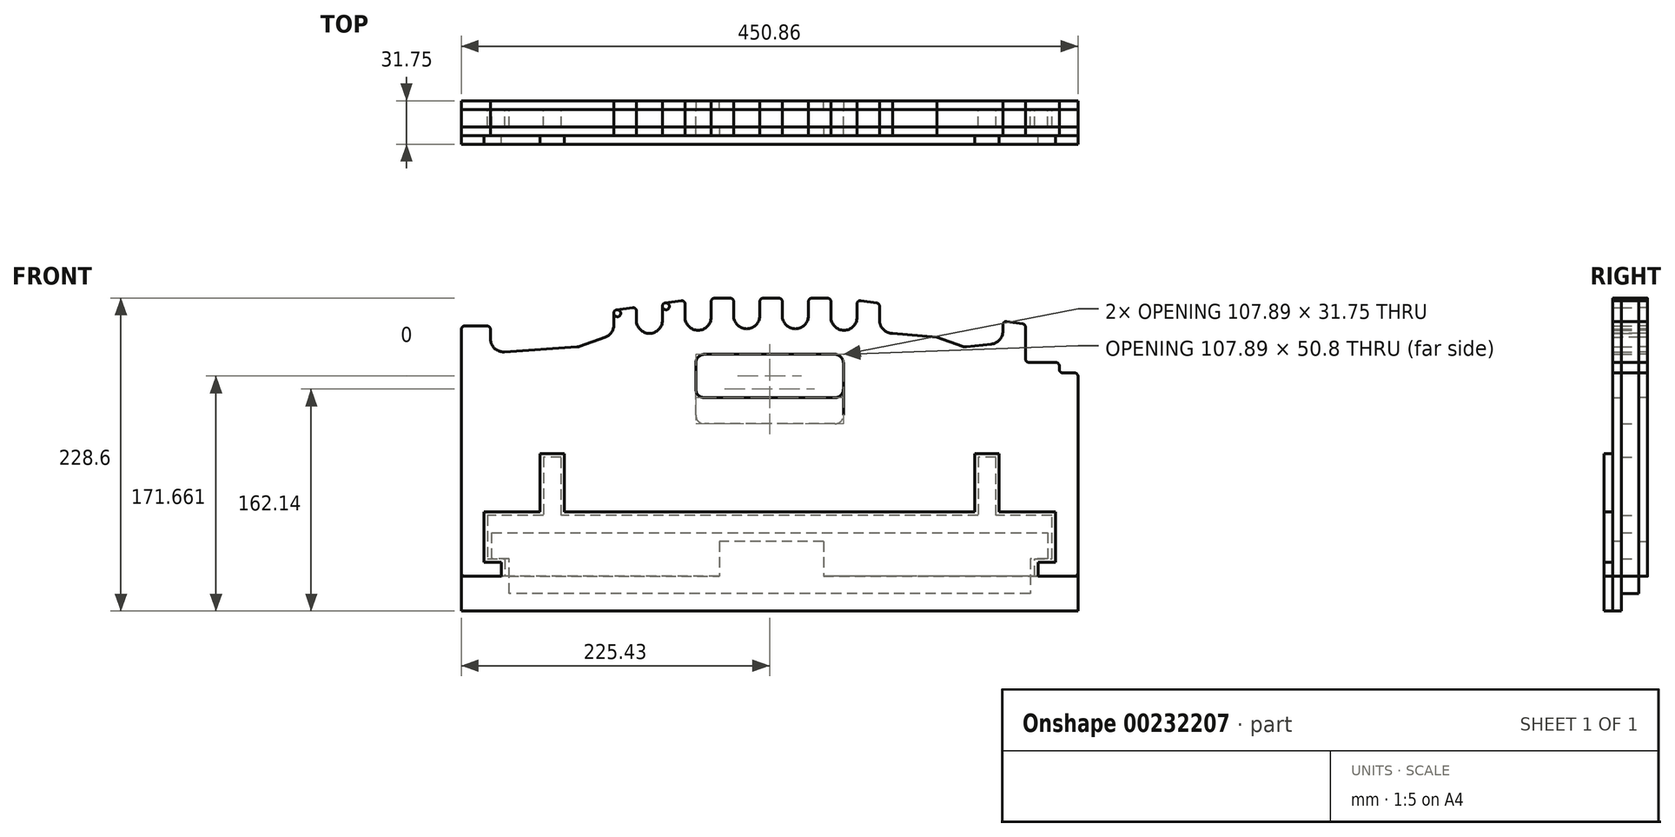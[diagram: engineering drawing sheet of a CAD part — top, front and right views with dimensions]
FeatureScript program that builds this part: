
annotation { "Feature Type Name" : "Feature", "Feature Type Description" : "" }
export const myFeature = defineFeature(function(context is Context, id is Id, definition is map)
    precondition{}
    {
        {
            var Q0;
            Q0=qCreatedBy(makeId("Front.planeOp"),FACE);
            var sketch = newSketch(context, id + "F0", { "sketchPlane" : qUnion([Q0])});
            skLineSegment(sketch, "E0", {"start": v(225.43, 44.45) * mm, "end": v(225.43, -101.6) * mm});
            skArc(sketch, "E1", {"start": v(225.42, 44.45) * mm, "mid": v(224.68, 46.25) * mm, "end": v(222.88, 47) * mm});
            skLineSegment(sketch, "E2", {"start": v(214.35, 47) * mm, "end": v(222.88, 47) * mm});
            skArc(sketch, "E3", {"start": v(211.8, 49.53) * mm, "mid": v(212.55, 47.73) * mm, "end": v(214.35, 47) * mm});
            skLineSegment(sketch, "E4", {"start": v(211.8, 52.07) * mm, "end": v(211.8, 49.53) * mm});
            skArc(sketch, "E5", {"start": v(211.8, 52.07) * mm, "mid": v(211.06, 53.87) * mm, "end": v(209.27, 54.6) * mm});
            skLineSegment(sketch, "E6", {"start": v(189.61, 54.61) * mm, "end": v(209.27, 54.61) * mm});
            skArc(sketch, "E7", {"start": v(187.07, 57.15) * mm, "mid": v(187.81, 55.35) * mm, "end": v(189.61, 54.61) * mm});
            skLineSegment(sketch, "E8", {"start": v(187.07, 80.43) * mm, "end": v(187.07, 57.15) * mm});
            skArc(sketch, "E9", {"start": v(187.07, 80.43) * mm, "mid": v(186.45, 82.1) * mm, "end": v(184.9, 82.94) * mm});
            skLineSegment(sketch, "E10", {"start": v(173.46, 84.58) * mm, "end": v(184.9, 82.94) * mm});
            skArc(sketch, "E11", {"start": v(173.46, 84.58) * mm, "mid": v(171.44, 83.98) * mm, "end": v(170.56, 82.06) * mm});
            skLineSegment(sketch, "E12", {"start": v(170.56, 77.52) * mm, "end": v(170.56, 82.06) * mm});
            skArc(sketch, "E13", {"start": v(162.11, 68.05) * mm, "mid": v(168.14, 71.17) * mm, "end": v(170.56, 77.52) * mm});
            skLineSegment(sketch, "E14", {"start": v(143.97, 65.99) * mm, "end": v(162.11, 68.05) * mm});
            skArc(sketch, "E15", {"start": v(141.12, 66.32) * mm, "mid": v(142.53, 65.99) * mm, "end": v(143.97, 65.99) * mm});
            skLineSegment(sketch, "E16", {"start": v(122.27, 73.06) * mm, "end": v(141.12, 66.32) * mm});
            skArc(sketch, "E17", {"start": v(115.95, 82.03) * mm, "mid": v(117.69, 76.54) * mm, "end": v(122.27, 73.06) * mm});
            skLineSegment(sketch, "E18", {"start": v(115.95, 90.6) * mm, "end": v(115.95, 82.03) * mm});
            skArc(sketch, "E19", {"start": v(115.95, 90.6) * mm, "mid": v(115.33, 92.26) * mm, "end": v(113.77, 93.1) * mm});
            skLineSegment(sketch, "E20", {"start": v(102.34, 94.74) * mm, "end": v(113.77, 93.1) * mm});
            skArc(sketch, "E21", {"start": v(102.34, 94.74) * mm, "mid": v(100.32, 94.14) * mm, "end": v(99.44, 92.22) * mm});
            skLineSegment(sketch, "E22", {"start": v(99.44, 85.4) * mm, "end": v(99.44, 92.22) * mm});
            skArc(sketch, "E23", {"start": v(80.4, 85.4) * mm, "mid": v(89.92, 75.87) * mm, "end": v(99.44, 85.4) * mm});
            skLineSegment(sketch, "E24", {"start": v(80.4, 95.67) * mm, "end": v(80.4, 85.4) * mm});
            skArc(sketch, "E25", {"start": v(80.4, 95.67) * mm, "mid": v(79.77, 97.34) * mm, "end": v(78.21, 98.19) * mm});
            skLineSegment(sketch, "E26", {"start": v(66.78, 99.82) * mm, "end": v(78.21, 98.19) * mm});
            skArc(sketch, "E27", {"start": v(66.78, 99.82) * mm, "mid": v(64.76, 99.22) * mm, "end": v(63.88, 97.3) * mm});
            skLineSegment(sketch, "E28", {"start": v(63.88, 87.64) * mm, "end": v(63.88, 97.3) * mm});
            skArc(sketch, "E29", {"start": v(44.83, 87.64) * mm, "mid": v(54.36, 78.12) * mm, "end": v(63.88, 87.64) * mm});
            skLineSegment(sketch, "E30", {"start": v(44.83, 99.06) * mm, "end": v(44.83, 87.64) * mm});
            skArc(sketch, "E31", {"start": v(44.83, 99.06) * mm, "mid": v(44.09, 100.86) * mm, "end": v(42.3, 101.6) * mm});
            skLineSegment(sketch, "E32", {"start": v(30.86, 101.6) * mm, "end": v(42.3, 101.6) * mm});
            skArc(sketch, "E33", {"start": v(30.86, 101.6) * mm, "mid": v(29.06, 100.86) * mm, "end": v(28.32, 99.06) * mm});
            skLineSegment(sketch, "E34", {"start": v(28.32, 88.76) * mm, "end": v(28.32, 99.06) * mm});
            skArc(sketch, "E35", {"start": v(9.27, 88.76) * mm, "mid": v(18.8, 79.24) * mm, "end": v(28.32, 88.76) * mm});
            skLineSegment(sketch, "E36", {"start": v(9.27, 99.06) * mm, "end": v(9.27, 88.76) * mm});
            skArc(sketch, "E37", {"start": v(9.27, 99.06) * mm, "mid": v(8.53, 100.86) * mm, "end": v(6.73, 101.6) * mm});
            skLineSegment(sketch, "E38", {"start": v(-4.7, 101.6) * mm, "end": v(6.73, 101.6) * mm});
            skArc(sketch, "E39", {"start": v(-4.7, 101.6) * mm, "mid": v(-6.5, 100.86) * mm, "end": v(-7.24, 99.06) * mm});
            skLineSegment(sketch, "E40", {"start": v(-7.24, 88.76) * mm, "end": v(-7.24, 99.06) * mm});
            skArc(sketch, "E41", {"start": v(-26.29, 88.76) * mm, "mid": v(-16.76, 79.24) * mm, "end": v(-7.24, 88.76) * mm});
            skLineSegment(sketch, "E42", {"start": v(-26.29, 99.06) * mm, "end": v(-26.29, 88.76) * mm});
            skArc(sketch, "E43", {"start": v(-26.29, 99.06) * mm, "mid": v(-27.03, 100.86) * mm, "end": v(-28.83, 101.6) * mm});
            skLineSegment(sketch, "E44", {"start": v(-40.26, 101.6) * mm, "end": v(-28.83, 101.6) * mm});
            skArc(sketch, "E45", {"start": v(-40.26, 101.6) * mm, "mid": v(-42.06, 100.86) * mm, "end": v(-42.8, 99.06) * mm});
            skLineSegment(sketch, "E46", {"start": v(-42.8, 87.64) * mm, "end": v(-42.8, 99.06) * mm});
            skArc(sketch, "E47", {"start": v(-61.85, 87.64) * mm, "mid": v(-52.32, 78.12) * mm, "end": v(-42.8, 87.64) * mm});
            skLineSegment(sketch, "E48", {"start": v(-61.85, 97.3) * mm, "end": v(-61.85, 87.64) * mm});
            skArc(sketch, "E49", {"start": v(-61.85, 97.3) * mm, "mid": v(-62.72, 99.23) * mm, "end": v(-64.75, 99.82) * mm});
            skLineSegment(sketch, "E50", {"start": v(-76.18, 98.19) * mm, "end": v(-64.75, 99.82) * mm});
            skArc(sketch, "E51", {"start": v(-76.18, 98.19) * mm, "mid": v(-77.74, 97.34) * mm, "end": v(-78.36, 95.67) * mm});
            skLineSegment(sketch, "E52", {"start": v(-78.36, 85.4) * mm, "end": v(-78.36, 95.67) * mm});
            skArc(sketch, "E53", {"start": v(-97.4, 85.4) * mm, "mid": v(-87.88, 75.87) * mm, "end": v(-78.36, 85.4) * mm});
            skLineSegment(sketch, "E54", {"start": v(-97.4, 92.23) * mm, "end": v(-97.4, 85.4) * mm});
            skArc(sketch, "E55", {"start": v(-97.4, 92.23) * mm, "mid": v(-98.28, 94.15) * mm, "end": v(-100.3, 94.74) * mm});
            skLineSegment(sketch, "E56", {"start": v(-111.74, 93.1) * mm, "end": v(-100.3, 94.74) * mm});
            skArc(sketch, "E57", {"start": v(-111.74, 93.1) * mm, "mid": v(-113.3, 92.26) * mm, "end": v(-113.92, 90.6) * mm});
            skLineSegment(sketch, "E58", {"start": v(-113.92, 82.03) * mm, "end": v(-113.92, 90.6) * mm});
            skArc(sketch, "E59", {"start": v(-120.24, 73.06) * mm, "mid": v(-115.66, 76.54) * mm, "end": v(-113.92, 82.03) * mm});
            skLineSegment(sketch, "E60", {"start": v(-139.09, 66.32) * mm, "end": v(-120.24, 73.06) * mm});
            skArc(sketch, "E61", {"start": v(-140.8, 65.96) * mm, "mid": v(-139.93, 66.08) * mm, "end": v(-139.09, 66.32) * mm});
            skLineSegment(sketch, "E62", {"start": v(-193.92, 62.35) * mm, "end": v(-140.8, 65.96) * mm});
            skArc(sketch, "E63", {"start": v(-204.09, 71.85) * mm, "mid": v(-201.07, 64.9) * mm, "end": v(-193.92, 62.35) * mm});
            skLineSegment(sketch, "E64", {"start": v(-204.09, 78.74) * mm, "end": v(-204.09, 71.85) * mm});
            skArc(sketch, "E65", {"start": v(-204.09, 78.74) * mm, "mid": v(-204.83, 80.54) * mm, "end": v(-206.63, 81.28) * mm});
            skLineSegment(sketch, "E66", {"start": v(-222.89, 81.28) * mm, "end": v(-206.63, 81.28) * mm});
            skArc(sketch, "E67", {"start": v(-222.89, 81.28) * mm, "mid": v(-224.68, 80.54) * mm, "end": v(-225.43, 78.74) * mm});
            skLineSegment(sketch, "E68", {"start": v(-225.43, -101.6) * mm, "end": v(-225.43, 78.74) * mm});
            skLineSegment(sketch, "E69", {"start": v(-193.68, -101.6) * mm, "end": v(-225.43, -101.6) * mm});
            skLineSegment(sketch, "E70", {"start": v(-193.68, -88.9) * mm, "end": v(-193.68, -101.6) * mm});
            skLineSegment(sketch, "E71", {"start": v(-206.38, -88.9) * mm, "end": v(-193.68, -88.9) * mm});
            skLineSegment(sketch, "E72", {"start": v(-206.38, -57.15) * mm, "end": v(-206.38, -88.9) * mm});
            skLineSegment(sketch, "E73", {"start": v(-165.35, -57.15) * mm, "end": v(-206.38, -57.15) * mm});
            skLineSegment(sketch, "E74", {"start": v(-165.35, -14.48) * mm, "end": v(-165.35, -57.15) * mm});
            skLineSegment(sketch, "E75", {"start": v(-152.4, -14.48) * mm, "end": v(-165.35, -14.48) * mm});
            skLineSegment(sketch, "E76", {"start": v(-152.4, -57.15) * mm, "end": v(-152.4, -14.48) * mm});
            skLineSegment(sketch, "E77", {"start": v(152.4, -57.15) * mm, "end": v(-152.4, -57.15) * mm});
            skLineSegment(sketch, "E78", {"start": v(152.4, -14.48) * mm, "end": v(152.4, -57.15) * mm});
            skLineSegment(sketch, "E79", {"start": v(165.35, -14.48) * mm, "end": v(152.4, -14.48) * mm});
            skLineSegment(sketch, "E80", {"start": v(165.35, -57.15) * mm, "end": v(165.35, -14.48) * mm});
            skLineSegment(sketch, "E81", {"start": v(206.38, -57.15) * mm, "end": v(165.35, -57.15) * mm});
            skLineSegment(sketch, "E82", {"start": v(206.38, -88.9) * mm, "end": v(206.38, -57.15) * mm});
            skLineSegment(sketch, "E83", {"start": v(193.68, -88.9) * mm, "end": v(206.38, -88.9) * mm});
            skLineSegment(sketch, "E84", {"start": v(193.68, -101.6) * mm, "end": v(193.68, -88.9) * mm});
            skLineSegment(sketch, "E85", {"start": v(225.43, -101.6) * mm, "end": v(193.68, -101.6) * mm});
            skLineSegment(sketch, "E86", {"start": v(47.6, 9.74) * mm, "end": v(-47.6, 9.74) * mm});
            skArc(sketch, "E87", {"start": v(-53.95, 16.1) * mm, "mid": v(-52.09, 11.6) * mm, "end": v(-47.6, 9.74) * mm});
            skLineSegment(sketch, "E88", {"start": v(-53.95, 16.1) * mm, "end": v(-53.95, 54.2) * mm});
            skArc(sketch, "E89", {"start": v(-47.6, 60.54) * mm, "mid": v(-52.09, 58.68) * mm, "end": v(-53.95, 54.2) * mm});
            skLineSegment(sketch, "E90", {"start": v(-47.6, 60.54) * mm, "end": v(47.6, 60.54) * mm});
            skArc(sketch, "E91", {"start": v(53.95, 54.2) * mm, "mid": v(52.09, 58.68) * mm, "end": v(47.6, 60.54) * mm});
            skLineSegment(sketch, "E92", {"start": v(53.95, 54.2) * mm, "end": v(53.95, 16.1) * mm});
            skArc(sketch, "E93", {"start": v(47.6, 9.74) * mm, "mid": v(52.09, 11.6) * mm, "end": v(53.95, 16.1) * mm});
            skLineSegment(sketch, "E94", {"start": v(225.43, -101.6) * mm, "end": v(-225.43, -101.6) * mm, "construction": true});
            skLineSegment(sketch, "E95", {"start": v(-225.43, -101.6) * mm, "end": v(-225.43, 0) * mm, "construction": true});
            skLineSegment(sketch, "E96", {"start": v(-225.43, 0) * mm, "end": v(225.43, 0) * mm, "construction": true});
            skLineSegment(sketch, "E97", {"start": v(225.43, 0) * mm, "end": v(225.43, -101.6) * mm, "construction": true});
            skSolve(sketch);
        }
        {
            var Q0;
            Q0 = qSketchRegion(id + "F0", true);
            extrude(context, id + "F1", {"entities" : qUnion([Q0]), "depth" : 12.7 * mm});
        }
        {
            var Q0;
            Q0=makeQuery(id+"F1.opExtrude","CAP_FACE",FACE,{"disambiguationData":[OSD([sQuery(id+"F0.wireOp",EDGE,"f3b8bc04-095d-494a-bcce-8306202adf07"),sQuery(id+"F0.wireOp",EDGE,"08e92012-2e21-4d94-9f0a-c8e57075e395"),sQuery(id+"F0.wireOp",EDGE,"122fa739-26d1-4298-ae19-82ac91bd4e23"),sQuery(id+"F0.wireOp",EDGE,"d5e32c5b-27bd-42dd-9b3f-d947ba78b5c6"),sQuery(id+"F0.wireOp",EDGE,"E0"),sQuery(id+"F0.wireOp",EDGE,"E1"),sQuery(id+"F0.wireOp",EDGE,"E2"),sQuery(id+"F0.wireOp",EDGE,"E3"),sQuery(id+"F0.wireOp",EDGE,"E4"),sQuery(id+"F0.wireOp",EDGE,"E5"),sQuery(id+"F0.wireOp",EDGE,"E6"),sQuery(id+"F0.wireOp",EDGE,"E7"),sQuery(id+"F0.wireOp",EDGE,"E8"),sQuery(id+"F0.wireOp",EDGE,"E9"),sQuery(id+"F0.wireOp",EDGE,"E10"),sQuery(id+"F0.wireOp",EDGE,"E11"),sQuery(id+"F0.wireOp",EDGE,"E12"),sQuery(id+"F0.wireOp",EDGE,"E13"),sQuery(id+"F0.wireOp",EDGE,"E14"),sQuery(id+"F0.wireOp",EDGE,"E15"),sQuery(id+"F0.wireOp",EDGE,"E16"),sQuery(id+"F0.wireOp",EDGE,"E17"),sQuery(id+"F0.wireOp",EDGE,"E18"),sQuery(id+"F0.wireOp",EDGE,"E19"),sQuery(id+"F0.wireOp",EDGE,"E20"),sQuery(id+"F0.wireOp",EDGE,"E21"),sQuery(id+"F0.wireOp",EDGE,"E22"),sQuery(id+"F0.wireOp",EDGE,"E23"),sQuery(id+"F0.wireOp",EDGE,"E24"),sQuery(id+"F0.wireOp",EDGE,"E25"),sQuery(id+"F0.wireOp",EDGE,"E26"),sQuery(id+"F0.wireOp",EDGE,"E27"),sQuery(id+"F0.wireOp",EDGE,"E28"),sQuery(id+"F0.wireOp",EDGE,"E29"),sQuery(id+"F0.wireOp",EDGE,"E30"),sQuery(id+"F0.wireOp",EDGE,"E31"),sQuery(id+"F0.wireOp",EDGE,"E32"),sQuery(id+"F0.wireOp",EDGE,"E33"),sQuery(id+"F0.wireOp",EDGE,"E34"),sQuery(id+"F0.wireOp",EDGE,"E35"),sQuery(id+"F0.wireOp",EDGE,"E36"),sQuery(id+"F0.wireOp",EDGE,"E37"),sQuery(id+"F0.wireOp",EDGE,"E38"),sQuery(id+"F0.wireOp",EDGE,"E39"),sQuery(id+"F0.wireOp",EDGE,"E40"),sQuery(id+"F0.wireOp",EDGE,"E41"),sQuery(id+"F0.wireOp",EDGE,"E42"),sQuery(id+"F0.wireOp",EDGE,"E43"),sQuery(id+"F0.wireOp",EDGE,"E44"),sQuery(id+"F0.wireOp",EDGE,"E45"),sQuery(id+"F0.wireOp",EDGE,"E46"),sQuery(id+"F0.wireOp",EDGE,"E47"),sQuery(id+"F0.wireOp",EDGE,"E48"),sQuery(id+"F0.wireOp",EDGE,"E49"),sQuery(id+"F0.wireOp",EDGE,"E50"),sQuery(id+"F0.wireOp",EDGE,"E51"),sQuery(id+"F0.wireOp",EDGE,"E52"),sQuery(id+"F0.wireOp",EDGE,"E53"),sQuery(id+"F0.wireOp",EDGE,"E54"),sQuery(id+"F0.wireOp",EDGE,"E55"),sQuery(id+"F0.wireOp",EDGE,"E56"),sQuery(id+"F0.wireOp",EDGE,"E57"),sQuery(id+"F0.wireOp",EDGE,"E58"),sQuery(id+"F0.wireOp",EDGE,"E59"),sQuery(id+"F0.wireOp",EDGE,"E60"),sQuery(id+"F0.wireOp",EDGE,"E61"),sQuery(id+"F0.wireOp",EDGE,"E62"),sQuery(id+"F0.wireOp",EDGE,"E63"),sQuery(id+"F0.wireOp",EDGE,"E64"),sQuery(id+"F0.wireOp",EDGE,"E65"),sQuery(id+"F0.wireOp",EDGE,"E66"),sQuery(id+"F0.wireOp",EDGE,"E67"),sQuery(id+"F0.wireOp",EDGE,"E68"),sQuery(id+"F0.wireOp",EDGE,"E69"),sQuery(id+"F0.wireOp",EDGE,"E70"),sQuery(id+"F0.wireOp",EDGE,"E71"),sQuery(id+"F0.wireOp",EDGE,"E72"),sQuery(id+"F0.wireOp",EDGE,"E73"),sQuery(id+"F0.wireOp",EDGE,"E74"),sQuery(id+"F0.wireOp",EDGE,"E75"),sQuery(id+"F0.wireOp",EDGE,"E76"),sQuery(id+"F0.wireOp",EDGE,"E77"),sQuery(id+"F0.wireOp",EDGE,"E78"),sQuery(id+"F0.wireOp",EDGE,"E79"),sQuery(id+"F0.wireOp",EDGE,"E80"),sQuery(id+"F0.wireOp",EDGE,"E81"),sQuery(id+"F0.wireOp",EDGE,"E82"),sQuery(id+"F0.wireOp",EDGE,"E83"),sQuery(id+"F0.wireOp",EDGE,"E84"),sQuery(id+"F0.wireOp",EDGE,"E85"),sQuery(id+"F0.wireOp",EDGE,"2d70706d-4c91-45b7-b293-bf747273fc1e"),sQuery(id+"F0.wireOp",EDGE,"f606c3c6-6e26-49ba-bb4a-ffbf22b89f78"),sQuery(id+"F0.wireOp",EDGE,"6ded5a20-7a3f-46e3-8459-1bb58dbc2f72"),sQuery(id+"F0.wireOp",EDGE,"099ca5a8-81e7-49d1-b38d-3a86f93f5891"),sQuery(id+"F0.wireOp",EDGE,"E86"),sQuery(id+"F0.wireOp",EDGE,"E87"),sQuery(id+"F0.wireOp",EDGE,"E88"),sQuery(id+"F0.wireOp",EDGE,"E89"),sQuery(id+"F0.wireOp",EDGE,"E90"),sQuery(id+"F0.wireOp",EDGE,"E91"),sQuery(id+"F0.wireOp",EDGE,"E92"),sQuery(id+"F0.wireOp",EDGE,"E93")])],"isStart":true});
            cPlane(context, id + "F2", {"entities" : qUnion([Q0]), "cplaneType" : CPlaneType.OFFSET, "offset" : 0 * mm, "oppositeDirection" : true, "width" : 152.4 * mm, "height" : 152.4 * mm});
        }
        {
            var Q0;
            Q0=qCreatedBy(id+"F2.planeOp",FACE);
            var sketch = newSketch(context, id + "F3", { "sketchPlane" : qUnion([Q0])});
            skLineSegment(sketch, "E98", {"start": v(-203.2, -69.85) * mm, "end": v(-203.2, -88.9) * mm});
            skLineSegment(sketch, "E99", {"start": v(-203.2, -88.9) * mm, "end": v(-190.5, -88.9) * mm});
            skLineSegment(sketch, "E100", {"start": v(-190.5, -88.9) * mm, "end": v(-190.5, -114.3) * mm});
            skLineSegment(sketch, "E101", {"start": v(-190.5, -114.3) * mm, "end": v(190.5, -114.3) * mm});
            skLineSegment(sketch, "E102", {"start": v(190.5, -114.3) * mm, "end": v(190.5, -88.9) * mm});
            skLineSegment(sketch, "E103", {"start": v(190.5, -88.9) * mm, "end": v(203.2, -88.9) * mm});
            skLineSegment(sketch, "E104", {"start": v(203.2, -88.9) * mm, "end": v(203.2, -69.85) * mm});
            skLineSegment(sketch, "E105", {"start": v(203.2, -69.85) * mm, "end": v(-203.2, -69.85) * mm});
            skSolve(sketch);
        }
        {
            var Q0;
            Q0 = qSketchRegion(id + "F3", true);
            extrude(context, id + "F4", {"entities" : qUnion([Q0]), "oppositeDirection" : true, "depth" : 12.7 * mm});
        }
        {
            var Q0;
            Q0=makeQuery(id+"F1.opExtrude","CAP_FACE",FACE,{"disambiguationData":[OSD([sQuery(id+"F0.wireOp",EDGE,"f3b8bc04-095d-494a-bcce-8306202adf07"),sQuery(id+"F0.wireOp",EDGE,"08e92012-2e21-4d94-9f0a-c8e57075e395"),sQuery(id+"F0.wireOp",EDGE,"122fa739-26d1-4298-ae19-82ac91bd4e23"),sQuery(id+"F0.wireOp",EDGE,"d5e32c5b-27bd-42dd-9b3f-d947ba78b5c6"),sQuery(id+"F0.wireOp",EDGE,"E0"),sQuery(id+"F0.wireOp",EDGE,"E1"),sQuery(id+"F0.wireOp",EDGE,"E2"),sQuery(id+"F0.wireOp",EDGE,"E3"),sQuery(id+"F0.wireOp",EDGE,"E4"),sQuery(id+"F0.wireOp",EDGE,"E5"),sQuery(id+"F0.wireOp",EDGE,"E6"),sQuery(id+"F0.wireOp",EDGE,"E7"),sQuery(id+"F0.wireOp",EDGE,"E8"),sQuery(id+"F0.wireOp",EDGE,"E9"),sQuery(id+"F0.wireOp",EDGE,"E10"),sQuery(id+"F0.wireOp",EDGE,"E11"),sQuery(id+"F0.wireOp",EDGE,"E12"),sQuery(id+"F0.wireOp",EDGE,"E13"),sQuery(id+"F0.wireOp",EDGE,"E14"),sQuery(id+"F0.wireOp",EDGE,"E15"),sQuery(id+"F0.wireOp",EDGE,"E16"),sQuery(id+"F0.wireOp",EDGE,"E17"),sQuery(id+"F0.wireOp",EDGE,"E18"),sQuery(id+"F0.wireOp",EDGE,"E19"),sQuery(id+"F0.wireOp",EDGE,"E20"),sQuery(id+"F0.wireOp",EDGE,"E21"),sQuery(id+"F0.wireOp",EDGE,"E22"),sQuery(id+"F0.wireOp",EDGE,"E23"),sQuery(id+"F0.wireOp",EDGE,"E24"),sQuery(id+"F0.wireOp",EDGE,"E25"),sQuery(id+"F0.wireOp",EDGE,"E26"),sQuery(id+"F0.wireOp",EDGE,"E27"),sQuery(id+"F0.wireOp",EDGE,"E28"),sQuery(id+"F0.wireOp",EDGE,"E29"),sQuery(id+"F0.wireOp",EDGE,"E30"),sQuery(id+"F0.wireOp",EDGE,"E31"),sQuery(id+"F0.wireOp",EDGE,"E32"),sQuery(id+"F0.wireOp",EDGE,"E33"),sQuery(id+"F0.wireOp",EDGE,"E34"),sQuery(id+"F0.wireOp",EDGE,"E35"),sQuery(id+"F0.wireOp",EDGE,"E36"),sQuery(id+"F0.wireOp",EDGE,"E37"),sQuery(id+"F0.wireOp",EDGE,"E38"),sQuery(id+"F0.wireOp",EDGE,"E39"),sQuery(id+"F0.wireOp",EDGE,"E40"),sQuery(id+"F0.wireOp",EDGE,"E41"),sQuery(id+"F0.wireOp",EDGE,"E42"),sQuery(id+"F0.wireOp",EDGE,"E43"),sQuery(id+"F0.wireOp",EDGE,"E44"),sQuery(id+"F0.wireOp",EDGE,"E45"),sQuery(id+"F0.wireOp",EDGE,"E46"),sQuery(id+"F0.wireOp",EDGE,"E47"),sQuery(id+"F0.wireOp",EDGE,"E48"),sQuery(id+"F0.wireOp",EDGE,"E49"),sQuery(id+"F0.wireOp",EDGE,"E50"),sQuery(id+"F0.wireOp",EDGE,"E51"),sQuery(id+"F0.wireOp",EDGE,"E52"),sQuery(id+"F0.wireOp",EDGE,"E53"),sQuery(id+"F0.wireOp",EDGE,"E54"),sQuery(id+"F0.wireOp",EDGE,"E55"),sQuery(id+"F0.wireOp",EDGE,"E56"),sQuery(id+"F0.wireOp",EDGE,"E57"),sQuery(id+"F0.wireOp",EDGE,"E58"),sQuery(id+"F0.wireOp",EDGE,"E59"),sQuery(id+"F0.wireOp",EDGE,"E60"),sQuery(id+"F0.wireOp",EDGE,"E61"),sQuery(id+"F0.wireOp",EDGE,"E62"),sQuery(id+"F0.wireOp",EDGE,"E63"),sQuery(id+"F0.wireOp",EDGE,"E64"),sQuery(id+"F0.wireOp",EDGE,"E65"),sQuery(id+"F0.wireOp",EDGE,"E66"),sQuery(id+"F0.wireOp",EDGE,"E67"),sQuery(id+"F0.wireOp",EDGE,"E68"),sQuery(id+"F0.wireOp",EDGE,"E69"),sQuery(id+"F0.wireOp",EDGE,"E70"),sQuery(id+"F0.wireOp",EDGE,"E71"),sQuery(id+"F0.wireOp",EDGE,"E72"),sQuery(id+"F0.wireOp",EDGE,"E73"),sQuery(id+"F0.wireOp",EDGE,"E74"),sQuery(id+"F0.wireOp",EDGE,"E75"),sQuery(id+"F0.wireOp",EDGE,"E76"),sQuery(id+"F0.wireOp",EDGE,"E77"),sQuery(id+"F0.wireOp",EDGE,"E78"),sQuery(id+"F0.wireOp",EDGE,"E79"),sQuery(id+"F0.wireOp",EDGE,"E80"),sQuery(id+"F0.wireOp",EDGE,"E81"),sQuery(id+"F0.wireOp",EDGE,"E82"),sQuery(id+"F0.wireOp",EDGE,"E83"),sQuery(id+"F0.wireOp",EDGE,"E84"),sQuery(id+"F0.wireOp",EDGE,"E85"),sQuery(id+"F0.wireOp",EDGE,"2d70706d-4c91-45b7-b293-bf747273fc1e"),sQuery(id+"F0.wireOp",EDGE,"f606c3c6-6e26-49ba-bb4a-ffbf22b89f78"),sQuery(id+"F0.wireOp",EDGE,"6ded5a20-7a3f-46e3-8459-1bb58dbc2f72"),sQuery(id+"F0.wireOp",EDGE,"099ca5a8-81e7-49d1-b38d-3a86f93f5891"),sQuery(id+"F0.wireOp",EDGE,"E86"),sQuery(id+"F0.wireOp",EDGE,"E87"),sQuery(id+"F0.wireOp",EDGE,"E88"),sQuery(id+"F0.wireOp",EDGE,"E89"),sQuery(id+"F0.wireOp",EDGE,"E90"),sQuery(id+"F0.wireOp",EDGE,"E91"),sQuery(id+"F0.wireOp",EDGE,"E92"),sQuery(id+"F0.wireOp",EDGE,"E93")])],"isStart":true});
            cPlane(context, id + "F5", {"entities" : qUnion([Q0]), "cplaneType" : CPlaneType.OFFSET, "offset" : 6.35 * mm, "oppositeDirection" : true, "width" : 152.4 * mm, "height" : 152.4 * mm});
        }
        {
            var Q0;
            Q0=qCreatedBy(id+"F2.planeOp",FACE);
            var sketch = newSketch(context, id + "F6", { "sketchPlane" : qUnion([Q0])});
            skLineSegment(sketch, "E106", {"start": v(-225.43, 44.45) * mm, "end": v(-225.43, -99.06) * mm});
            skArc(sketch, "E107", {"start": v(-225.43, -99.06) * mm, "mid": v(-224.68, -100.86) * mm, "end": v(-222.89, -101.6) * mm});
            skLineSegment(sketch, "E108", {"start": v(-222.89, -101.6) * mm, "end": v(222.88, -101.6) * mm});
            skArc(sketch, "E109", {"start": v(222.88, -101.6) * mm, "mid": v(224.68, -100.86) * mm, "end": v(225.42, -99.06) * mm});
            skLineSegment(sketch, "E110", {"start": v(225.43, -99.06) * mm, "end": v(225.43, 78.74) * mm});
            skArc(sketch, "E111", {"start": v(225.42, 78.74) * mm, "mid": v(224.68, 80.54) * mm, "end": v(222.88, 81.28) * mm});
            skLineSegment(sketch, "E112", {"start": v(222.88, 81.28) * mm, "end": v(206.63, 81.28) * mm});
            skArc(sketch, "E113", {"start": v(206.63, 81.28) * mm, "mid": v(204.83, 80.54) * mm, "end": v(204.09, 78.74) * mm});
            skLineSegment(sketch, "E114", {"start": v(204.09, 78.74) * mm, "end": v(204.09, 71.85) * mm});
            skArc(sketch, "E115", {"start": v(193.92, 62.35) * mm, "mid": v(201.07, 64.9) * mm, "end": v(204.09, 71.85) * mm});
            skLineSegment(sketch, "E116", {"start": v(193.92, 62.35) * mm, "end": v(140.8, 65.96) * mm});
            skArc(sketch, "E117", {"start": v(139.09, 66.32) * mm, "mid": v(139.93, 66.08) * mm, "end": v(140.8, 65.96) * mm});
            skLineSegment(sketch, "E118", {"start": v(139.09, 66.32) * mm, "end": v(120.24, 73.06) * mm});
            skArc(sketch, "E119", {"start": v(113.92, 82.03) * mm, "mid": v(115.66, 76.54) * mm, "end": v(120.24, 73.06) * mm});
            skLineSegment(sketch, "E120", {"start": v(113.92, 82.03) * mm, "end": v(113.92, 90.6) * mm});
            skArc(sketch, "E121", {"start": v(113.92, 90.6) * mm, "mid": v(113.3, 92.26) * mm, "end": v(111.74, 93.1) * mm});
            skLineSegment(sketch, "E122", {"start": v(111.74, 93.1) * mm, "end": v(100.3, 94.74) * mm});
            skArc(sketch, "E123", {"start": v(100.3, 94.74) * mm, "mid": v(98.28, 94.15) * mm, "end": v(97.4, 92.23) * mm});
            skLineSegment(sketch, "E124", {"start": v(97.4, 92.23) * mm, "end": v(97.4, 85.4) * mm});
            skArc(sketch, "E125", {"start": v(78.36, 85.4) * mm, "mid": v(87.88, 75.87) * mm, "end": v(97.4, 85.4) * mm});
            skLineSegment(sketch, "E126", {"start": v(78.36, 85.4) * mm, "end": v(78.36, 95.67) * mm});
            skArc(sketch, "E127", {"start": v(78.36, 95.67) * mm, "mid": v(77.74, 97.34) * mm, "end": v(76.18, 98.19) * mm});
            skLineSegment(sketch, "E128", {"start": v(76.18, 98.19) * mm, "end": v(64.75, 99.82) * mm});
            skArc(sketch, "E129", {"start": v(64.75, 99.82) * mm, "mid": v(62.72, 99.23) * mm, "end": v(61.85, 97.3) * mm});
            skLineSegment(sketch, "E130", {"start": v(61.85, 97.3) * mm, "end": v(61.85, 87.64) * mm});
            skArc(sketch, "E131", {"start": v(42.8, 87.64) * mm, "mid": v(52.32, 78.12) * mm, "end": v(61.85, 87.64) * mm});
            skLineSegment(sketch, "E132", {"start": v(42.8, 87.64) * mm, "end": v(42.8, 99.06) * mm});
            skArc(sketch, "E133", {"start": v(42.8, 99.06) * mm, "mid": v(42.06, 100.86) * mm, "end": v(40.26, 101.6) * mm});
            skLineSegment(sketch, "E134", {"start": v(40.26, 101.6) * mm, "end": v(28.83, 101.6) * mm});
            skArc(sketch, "E135", {"start": v(28.83, 101.6) * mm, "mid": v(27.03, 100.86) * mm, "end": v(26.29, 99.06) * mm});
            skLineSegment(sketch, "E136", {"start": v(26.29, 99.06) * mm, "end": v(26.29, 88.76) * mm});
            skArc(sketch, "E137", {"start": v(7.24, 88.76) * mm, "mid": v(16.76, 79.24) * mm, "end": v(26.29, 88.76) * mm});
            skLineSegment(sketch, "E138", {"start": v(7.24, 88.76) * mm, "end": v(7.24, 99.06) * mm});
            skArc(sketch, "E139", {"start": v(7.24, 99.06) * mm, "mid": v(6.5, 100.86) * mm, "end": v(4.7, 101.6) * mm});
            skLineSegment(sketch, "E140", {"start": v(4.7, 101.6) * mm, "end": v(-6.73, 101.6) * mm});
            skArc(sketch, "E141", {"start": v(-6.73, 101.6) * mm, "mid": v(-8.53, 100.86) * mm, "end": v(-9.27, 99.06) * mm});
            skLineSegment(sketch, "E142", {"start": v(-9.27, 99.06) * mm, "end": v(-9.27, 88.76) * mm});
            skArc(sketch, "E143", {"start": v(-28.32, 88.76) * mm, "mid": v(-18.8, 79.24) * mm, "end": v(-9.27, 88.76) * mm});
            skLineSegment(sketch, "E144", {"start": v(-28.32, 88.76) * mm, "end": v(-28.32, 99.06) * mm});
            skArc(sketch, "E145", {"start": v(-28.32, 99.06) * mm, "mid": v(-29.06, 100.86) * mm, "end": v(-30.86, 101.6) * mm});
            skLineSegment(sketch, "E146", {"start": v(-30.86, 101.6) * mm, "end": v(-42.3, 101.6) * mm});
            skArc(sketch, "E147", {"start": v(-42.3, 101.6) * mm, "mid": v(-44.09, 100.86) * mm, "end": v(-44.83, 99.06) * mm});
            skLineSegment(sketch, "E148", {"start": v(-44.83, 99.06) * mm, "end": v(-44.83, 87.64) * mm});
            skArc(sketch, "E149", {"start": v(-63.88, 87.64) * mm, "mid": v(-54.36, 78.12) * mm, "end": v(-44.83, 87.64) * mm});
            skLineSegment(sketch, "E150", {"start": v(-63.88, 87.64) * mm, "end": v(-63.88, 97.3) * mm});
            skArc(sketch, "E151", {"start": v(-63.88, 97.3) * mm, "mid": v(-64.76, 99.22) * mm, "end": v(-66.78, 99.82) * mm});
            skLineSegment(sketch, "E152", {"start": v(-66.78, 99.82) * mm, "end": v(-78.21, 98.19) * mm});
            skArc(sketch, "E153", {"start": v(-78.21, 98.19) * mm, "mid": v(-79.77, 97.34) * mm, "end": v(-80.4, 95.67) * mm});
            skLineSegment(sketch, "E154", {"start": v(-80.4, 95.67) * mm, "end": v(-80.4, 85.4) * mm});
            skArc(sketch, "E155", {"start": v(-99.44, 85.4) * mm, "mid": v(-89.92, 75.87) * mm, "end": v(-80.4, 85.4) * mm});
            skLineSegment(sketch, "E156", {"start": v(-99.44, 85.4) * mm, "end": v(-99.44, 92.22) * mm});
            skArc(sketch, "E157", {"start": v(-99.44, 92.22) * mm, "mid": v(-100.32, 94.14) * mm, "end": v(-102.34, 94.74) * mm});
            skLineSegment(sketch, "E158", {"start": v(-102.34, 94.74) * mm, "end": v(-113.77, 93.1) * mm});
            skArc(sketch, "E159", {"start": v(-113.77, 93.1) * mm, "mid": v(-115.33, 92.26) * mm, "end": v(-115.95, 90.6) * mm});
            skLineSegment(sketch, "E160", {"start": v(-115.95, 90.6) * mm, "end": v(-115.95, 82.03) * mm});
            skArc(sketch, "E161", {"start": v(-122.27, 73.06) * mm, "mid": v(-117.69, 76.54) * mm, "end": v(-115.95, 82.03) * mm});
            skLineSegment(sketch, "E162", {"start": v(-122.27, 73.06) * mm, "end": v(-141.12, 66.32) * mm});
            skArc(sketch, "E163", {"start": v(-143.97, 65.99) * mm, "mid": v(-142.53, 65.99) * mm, "end": v(-141.12, 66.32) * mm});
            skLineSegment(sketch, "E164", {"start": v(-143.97, 65.99) * mm, "end": v(-162.11, 68.05) * mm});
            skArc(sketch, "E165", {"start": v(-170.56, 77.52) * mm, "mid": v(-168.14, 71.17) * mm, "end": v(-162.11, 68.05) * mm});
            skLineSegment(sketch, "E166", {"start": v(-170.56, 77.52) * mm, "end": v(-170.56, 82.06) * mm});
            skArc(sketch, "E167", {"start": v(-170.56, 82.06) * mm, "mid": v(-171.44, 83.98) * mm, "end": v(-173.46, 84.58) * mm});
            skLineSegment(sketch, "E168", {"start": v(-173.46, 84.58) * mm, "end": v(-184.9, 82.94) * mm});
            skArc(sketch, "E169", {"start": v(-184.9, 82.94) * mm, "mid": v(-186.45, 82.1) * mm, "end": v(-187.07, 80.43) * mm});
            skLineSegment(sketch, "E170", {"start": v(-187.07, 80.43) * mm, "end": v(-187.07, 57.15) * mm});
            skArc(sketch, "E171", {"start": v(-189.61, 54.61) * mm, "mid": v(-187.81, 55.35) * mm, "end": v(-187.07, 57.15) * mm});
            skLineSegment(sketch, "E172", {"start": v(-189.61, 54.61) * mm, "end": v(-209.27, 54.61) * mm});
            skArc(sketch, "E173", {"start": v(-209.27, 54.6) * mm, "mid": v(-211.06, 53.87) * mm, "end": v(-211.8, 52.07) * mm});
            skLineSegment(sketch, "E174", {"start": v(-211.8, 52.07) * mm, "end": v(-211.8, 49.53) * mm});
            skArc(sketch, "E175", {"start": v(-214.35, 47) * mm, "mid": v(-212.55, 47.73) * mm, "end": v(-211.8, 49.53) * mm});
            skLineSegment(sketch, "E176", {"start": v(-214.35, 47) * mm, "end": v(-222.89, 47) * mm});
            skArc(sketch, "E177", {"start": v(-222.89, 47) * mm, "mid": v(-224.68, 46.25) * mm, "end": v(-225.43, 44.45) * mm});
            skLineSegment(sketch, "E178", {"start": v(-47.6, 28.79) * mm, "end": v(47.6, 28.79) * mm});
            skArc(sketch, "E179", {"start": v(-53.95, 35.14) * mm, "mid": v(-52.09, 30.65) * mm, "end": v(-47.6, 28.79) * mm});
            skLineSegment(sketch, "E180", {"start": v(-53.95, 54.19) * mm, "end": v(-53.95, 35.14) * mm});
            skArc(sketch, "E181", {"start": v(-47.6, 60.54) * mm, "mid": v(-52.09, 58.68) * mm, "end": v(-53.95, 54.19) * mm});
            skLineSegment(sketch, "E182", {"start": v(47.6, 60.54) * mm, "end": v(-47.6, 60.54) * mm});
            skArc(sketch, "E183", {"start": v(53.95, 54.19) * mm, "mid": v(52.09, 58.68) * mm, "end": v(47.6, 60.54) * mm});
            skLineSegment(sketch, "E184", {"start": v(53.95, 35.14) * mm, "end": v(53.95, 54.19) * mm});
            skArc(sketch, "E185", {"start": v(47.6, 28.79) * mm, "mid": v(52.09, 30.65) * mm, "end": v(53.95, 35.14) * mm});
            skSolve(sketch);
        }
        {
            var Q0;
            Q0 = qSketchRegion(id + "F6", true);
            extrude(context, id + "F7", {"entities" : qUnion([Q0]), "depth" : 6.35 * mm});
        }
        {
            var Q0;
            Q0=makeQuery(id+"F7.opExtrude","CAP_FACE",FACE,{"disambiguationData":[OSD([sQuery(id+"F6.wireOp",EDGE,"765eaaff-3c03-4aed-97cd-0da59d786b2a"),sQuery(id+"F6.wireOp",EDGE,"bfbbba31-eefb-4337-b840-f57609f327d5"),sQuery(id+"F6.wireOp",EDGE,"d9fe1464-95a0-43a8-9d73-98f239073346"),sQuery(id+"F6.wireOp",EDGE,"3dbae0e5-671e-48e1-8151-e821474c8e52"),sQuery(id+"F6.wireOp",EDGE,"E106"),sQuery(id+"F6.wireOp",EDGE,"E107"),sQuery(id+"F6.wireOp",EDGE,"E108"),sQuery(id+"F6.wireOp",EDGE,"E109"),sQuery(id+"F6.wireOp",EDGE,"E110"),sQuery(id+"F6.wireOp",EDGE,"E111"),sQuery(id+"F6.wireOp",EDGE,"E112"),sQuery(id+"F6.wireOp",EDGE,"E113"),sQuery(id+"F6.wireOp",EDGE,"E114"),sQuery(id+"F6.wireOp",EDGE,"E115"),sQuery(id+"F6.wireOp",EDGE,"E116"),sQuery(id+"F6.wireOp",EDGE,"E117"),sQuery(id+"F6.wireOp",EDGE,"E118"),sQuery(id+"F6.wireOp",EDGE,"E119"),sQuery(id+"F6.wireOp",EDGE,"E120"),sQuery(id+"F6.wireOp",EDGE,"E121"),sQuery(id+"F6.wireOp",EDGE,"E122"),sQuery(id+"F6.wireOp",EDGE,"E123"),sQuery(id+"F6.wireOp",EDGE,"E124"),sQuery(id+"F6.wireOp",EDGE,"E125"),sQuery(id+"F6.wireOp",EDGE,"E126"),sQuery(id+"F6.wireOp",EDGE,"E127"),sQuery(id+"F6.wireOp",EDGE,"E128"),sQuery(id+"F6.wireOp",EDGE,"E129"),sQuery(id+"F6.wireOp",EDGE,"E130"),sQuery(id+"F6.wireOp",EDGE,"E131"),sQuery(id+"F6.wireOp",EDGE,"E132"),sQuery(id+"F6.wireOp",EDGE,"E133"),sQuery(id+"F6.wireOp",EDGE,"E134"),sQuery(id+"F6.wireOp",EDGE,"E135"),sQuery(id+"F6.wireOp",EDGE,"E136"),sQuery(id+"F6.wireOp",EDGE,"E137"),sQuery(id+"F6.wireOp",EDGE,"E138"),sQuery(id+"F6.wireOp",EDGE,"E139"),sQuery(id+"F6.wireOp",EDGE,"E140"),sQuery(id+"F6.wireOp",EDGE,"E141"),sQuery(id+"F6.wireOp",EDGE,"E142"),sQuery(id+"F6.wireOp",EDGE,"E143"),sQuery(id+"F6.wireOp",EDGE,"E144"),sQuery(id+"F6.wireOp",EDGE,"E145"),sQuery(id+"F6.wireOp",EDGE,"E146"),sQuery(id+"F6.wireOp",EDGE,"E147"),sQuery(id+"F6.wireOp",EDGE,"E148"),sQuery(id+"F6.wireOp",EDGE,"E149"),sQuery(id+"F6.wireOp",EDGE,"E150"),sQuery(id+"F6.wireOp",EDGE,"E151"),sQuery(id+"F6.wireOp",EDGE,"E152"),sQuery(id+"F6.wireOp",EDGE,"E153"),sQuery(id+"F6.wireOp",EDGE,"E154"),sQuery(id+"F6.wireOp",EDGE,"E155"),sQuery(id+"F6.wireOp",EDGE,"E156"),sQuery(id+"F6.wireOp",EDGE,"E157"),sQuery(id+"F6.wireOp",EDGE,"E158"),sQuery(id+"F6.wireOp",EDGE,"E159"),sQuery(id+"F6.wireOp",EDGE,"E160"),sQuery(id+"F6.wireOp",EDGE,"E161"),sQuery(id+"F6.wireOp",EDGE,"E162"),sQuery(id+"F6.wireOp",EDGE,"E163"),sQuery(id+"F6.wireOp",EDGE,"E164"),sQuery(id+"F6.wireOp",EDGE,"E165"),sQuery(id+"F6.wireOp",EDGE,"E166"),sQuery(id+"F6.wireOp",EDGE,"E167"),sQuery(id+"F6.wireOp",EDGE,"E168"),sQuery(id+"F6.wireOp",EDGE,"E169"),sQuery(id+"F6.wireOp",EDGE,"E170"),sQuery(id+"F6.wireOp",EDGE,"E171"),sQuery(id+"F6.wireOp",EDGE,"E172"),sQuery(id+"F6.wireOp",EDGE,"E173"),sQuery(id+"F6.wireOp",EDGE,"E174"),sQuery(id+"F6.wireOp",EDGE,"E175"),sQuery(id+"F6.wireOp",EDGE,"E176"),sQuery(id+"F6.wireOp",EDGE,"E177"),sQuery(id+"F6.wireOp",EDGE,"E178"),sQuery(id+"F6.wireOp",EDGE,"E179"),sQuery(id+"F6.wireOp",EDGE,"E180"),sQuery(id+"F6.wireOp",EDGE,"E181"),sQuery(id+"F6.wireOp",EDGE,"E182"),sQuery(id+"F6.wireOp",EDGE,"E183"),sQuery(id+"F6.wireOp",EDGE,"E184"),sQuery(id+"F6.wireOp",EDGE,"E185"),sQuery(id+"F6.wireOp",EDGE,"f9493e98-5abe-4126-86ac-bdb0b4f7d6da"),sQuery(id+"F6.wireOp",EDGE,"112f2961-29c0-47fd-bd17-f927e6cd5f86"),sQuery(id+"F6.wireOp",EDGE,"d182d45b-51f4-4f19-bbab-538119165d43"),sQuery(id+"F6.wireOp",EDGE,"f2dcc7ce-426b-4624-9908-b4b424994630")])],"isStart":false});
            var sketch = newSketch(context, id + "F8", { "sketchPlane" : qUnion([Q0])});
            skLineSegment(sketch, "E186", {"start": v(225.43, -92.22) * mm, "end": v(47.24, -92.22) * mm, "construction": true});
            skLineSegment(sketch, "E187", {"start": v(47.24, -92.22) * mm, "end": v(11.43, -92.22) * mm, "construction": true});
            skCircle(sketch, "E188", {"center": v(11.43, -92.22) * mm, "radius": 6.35 * mm, "construction": true});
            skLineSegment(sketch, "E189.bottom", {"start": v(-39.37, -76.2) * mm, "end": v(36.83, -76.2) * mm});
            skLineSegment(sketch, "E189.top", {"start": v(-39.37, -101.6) * mm, "end": v(36.83, -101.6) * mm});
            skLineSegment(sketch, "E189.left", {"start": v(-39.37, -76.2) * mm, "end": v(-39.37, -101.6) * mm});
            skLineSegment(sketch, "E189.right", {"start": v(36.83, -76.2) * mm, "end": v(36.83, -101.6) * mm});
            skLineSegment(sketch, "E190", {"start": v(11.43, -92.22) * mm, "end": v(-13.97, -92.22) * mm, "construction": true});
            skCircle(sketch, "E191", {"center": v(-13.97, -92.22) * mm, "radius": 6.35 * mm, "construction": true});
            skSolve(sketch);
        }
        {
            var Q0;
            Q0 = qSketchRegion(id + "F8", true);
            extrude(context, id + "F9", {"entities" : qUnion([Q0]), "operationType" : NewBodyOperationType.REMOVE, "oppositeDirection" : true, "depth" : 6.35 * mm});
        }
        {
            var Q0;
            Q0=makeQuery(id+"F7.opExtrude","SWEPT_BODY",BODY,{"disambiguationData":[OSD([sQuery(id+"F6.wireOp",EDGE,"765eaaff-3c03-4aed-97cd-0da59d786b2a"),sQuery(id+"F6.wireOp",EDGE,"bfbbba31-eefb-4337-b840-f57609f327d5"),sQuery(id+"F6.wireOp",EDGE,"d9fe1464-95a0-43a8-9d73-98f239073346"),sQuery(id+"F6.wireOp",EDGE,"3dbae0e5-671e-48e1-8151-e821474c8e52"),sQuery(id+"F6.wireOp",EDGE,"E106"),sQuery(id+"F6.wireOp",EDGE,"E107"),sQuery(id+"F6.wireOp",EDGE,"E108"),sQuery(id+"F6.wireOp",EDGE,"E109"),sQuery(id+"F6.wireOp",EDGE,"E110"),sQuery(id+"F6.wireOp",EDGE,"E111"),sQuery(id+"F6.wireOp",EDGE,"E112"),sQuery(id+"F6.wireOp",EDGE,"E113"),sQuery(id+"F6.wireOp",EDGE,"E114"),sQuery(id+"F6.wireOp",EDGE,"E115"),sQuery(id+"F6.wireOp",EDGE,"E116"),sQuery(id+"F6.wireOp",EDGE,"E117"),sQuery(id+"F6.wireOp",EDGE,"E118"),sQuery(id+"F6.wireOp",EDGE,"E119"),sQuery(id+"F6.wireOp",EDGE,"E120"),sQuery(id+"F6.wireOp",EDGE,"E121"),sQuery(id+"F6.wireOp",EDGE,"E122"),sQuery(id+"F6.wireOp",EDGE,"E123"),sQuery(id+"F6.wireOp",EDGE,"E124"),sQuery(id+"F6.wireOp",EDGE,"E125"),sQuery(id+"F6.wireOp",EDGE,"E126"),sQuery(id+"F6.wireOp",EDGE,"E127"),sQuery(id+"F6.wireOp",EDGE,"E128"),sQuery(id+"F6.wireOp",EDGE,"E129"),sQuery(id+"F6.wireOp",EDGE,"E130"),sQuery(id+"F6.wireOp",EDGE,"E131"),sQuery(id+"F6.wireOp",EDGE,"E132"),sQuery(id+"F6.wireOp",EDGE,"E133"),sQuery(id+"F6.wireOp",EDGE,"E134"),sQuery(id+"F6.wireOp",EDGE,"E135"),sQuery(id+"F6.wireOp",EDGE,"E136"),sQuery(id+"F6.wireOp",EDGE,"E137"),sQuery(id+"F6.wireOp",EDGE,"E138"),sQuery(id+"F6.wireOp",EDGE,"E139"),sQuery(id+"F6.wireOp",EDGE,"E140"),sQuery(id+"F6.wireOp",EDGE,"E141"),sQuery(id+"F6.wireOp",EDGE,"E142"),sQuery(id+"F6.wireOp",EDGE,"E143"),sQuery(id+"F6.wireOp",EDGE,"E144"),sQuery(id+"F6.wireOp",EDGE,"E145"),sQuery(id+"F6.wireOp",EDGE,"E146"),sQuery(id+"F6.wireOp",EDGE,"E147"),sQuery(id+"F6.wireOp",EDGE,"E148"),sQuery(id+"F6.wireOp",EDGE,"E149"),sQuery(id+"F6.wireOp",EDGE,"E150"),sQuery(id+"F6.wireOp",EDGE,"E151"),sQuery(id+"F6.wireOp",EDGE,"E152"),sQuery(id+"F6.wireOp",EDGE,"E153"),sQuery(id+"F6.wireOp",EDGE,"E154"),sQuery(id+"F6.wireOp",EDGE,"E155"),sQuery(id+"F6.wireOp",EDGE,"E156"),sQuery(id+"F6.wireOp",EDGE,"E157"),sQuery(id+"F6.wireOp",EDGE,"E158"),sQuery(id+"F6.wireOp",EDGE,"E159"),sQuery(id+"F6.wireOp",EDGE,"E160"),sQuery(id+"F6.wireOp",EDGE,"E161"),sQuery(id+"F6.wireOp",EDGE,"E162"),sQuery(id+"F6.wireOp",EDGE,"E163"),sQuery(id+"F6.wireOp",EDGE,"E164"),sQuery(id+"F6.wireOp",EDGE,"E165"),sQuery(id+"F6.wireOp",EDGE,"E166"),sQuery(id+"F6.wireOp",EDGE,"E167"),sQuery(id+"F6.wireOp",EDGE,"E168"),sQuery(id+"F6.wireOp",EDGE,"E169"),sQuery(id+"F6.wireOp",EDGE,"E170"),sQuery(id+"F6.wireOp",EDGE,"E171"),sQuery(id+"F6.wireOp",EDGE,"E172"),sQuery(id+"F6.wireOp",EDGE,"E173"),sQuery(id+"F6.wireOp",EDGE,"E174"),sQuery(id+"F6.wireOp",EDGE,"E175"),sQuery(id+"F6.wireOp",EDGE,"E176"),sQuery(id+"F6.wireOp",EDGE,"E177"),sQuery(id+"F6.wireOp",EDGE,"E178"),sQuery(id+"F6.wireOp",EDGE,"E179"),sQuery(id+"F6.wireOp",EDGE,"E180"),sQuery(id+"F6.wireOp",EDGE,"E181"),sQuery(id+"F6.wireOp",EDGE,"E182"),sQuery(id+"F6.wireOp",EDGE,"E183"),sQuery(id+"F6.wireOp",EDGE,"E184"),sQuery(id+"F6.wireOp",EDGE,"E185"),sQuery(id+"F6.wireOp",EDGE,"f9493e98-5abe-4126-86ac-bdb0b4f7d6da"),sQuery(id+"F6.wireOp",EDGE,"112f2961-29c0-47fd-bd17-f927e6cd5f86"),sQuery(id+"F6.wireOp",EDGE,"d182d45b-51f4-4f19-bbab-538119165d43"),sQuery(id+"F6.wireOp",EDGE,"f2dcc7ce-426b-4624-9908-b4b424994630")])]});
            var Q1;
            Q1=qCreatedBy(id+"F5.planeOp",FACE);
            mirror(context, id + "F10", {"entities" : qUnion([Q0]), "mirrorPlane" : qUnion([Q1])});
        }
        {
            var Q0;
            Q0=makeQuery(id+"F10.opPattern","COPY",FACE,{"derivedFrom":makeQuery(id+"F7.opExtrude","CAP_FACE",FACE,{"disambiguationData":[OSD([sQuery(id+"F6.wireOp",EDGE,"765eaaff-3c03-4aed-97cd-0da59d786b2a"),sQuery(id+"F6.wireOp",EDGE,"bfbbba31-eefb-4337-b840-f57609f327d5"),sQuery(id+"F6.wireOp",EDGE,"d9fe1464-95a0-43a8-9d73-98f239073346"),sQuery(id+"F6.wireOp",EDGE,"3dbae0e5-671e-48e1-8151-e821474c8e52"),sQuery(id+"F6.wireOp",EDGE,"E106"),sQuery(id+"F6.wireOp",EDGE,"E107"),sQuery(id+"F6.wireOp",EDGE,"E108"),sQuery(id+"F6.wireOp",EDGE,"E109"),sQuery(id+"F6.wireOp",EDGE,"E110"),sQuery(id+"F6.wireOp",EDGE,"E111"),sQuery(id+"F6.wireOp",EDGE,"E112"),sQuery(id+"F6.wireOp",EDGE,"E113"),sQuery(id+"F6.wireOp",EDGE,"E114"),sQuery(id+"F6.wireOp",EDGE,"E115"),sQuery(id+"F6.wireOp",EDGE,"E116"),sQuery(id+"F6.wireOp",EDGE,"E117"),sQuery(id+"F6.wireOp",EDGE,"E118"),sQuery(id+"F6.wireOp",EDGE,"E119"),sQuery(id+"F6.wireOp",EDGE,"E120"),sQuery(id+"F6.wireOp",EDGE,"E121"),sQuery(id+"F6.wireOp",EDGE,"E122"),sQuery(id+"F6.wireOp",EDGE,"E123"),sQuery(id+"F6.wireOp",EDGE,"E124"),sQuery(id+"F6.wireOp",EDGE,"E125"),sQuery(id+"F6.wireOp",EDGE,"E126"),sQuery(id+"F6.wireOp",EDGE,"E127"),sQuery(id+"F6.wireOp",EDGE,"E128"),sQuery(id+"F6.wireOp",EDGE,"E129"),sQuery(id+"F6.wireOp",EDGE,"E130"),sQuery(id+"F6.wireOp",EDGE,"E131"),sQuery(id+"F6.wireOp",EDGE,"E132"),sQuery(id+"F6.wireOp",EDGE,"E133"),sQuery(id+"F6.wireOp",EDGE,"E134"),sQuery(id+"F6.wireOp",EDGE,"E135"),sQuery(id+"F6.wireOp",EDGE,"E136"),sQuery(id+"F6.wireOp",EDGE,"E137"),sQuery(id+"F6.wireOp",EDGE,"E138"),sQuery(id+"F6.wireOp",EDGE,"E139"),sQuery(id+"F6.wireOp",EDGE,"E140"),sQuery(id+"F6.wireOp",EDGE,"E141"),sQuery(id+"F6.wireOp",EDGE,"E142"),sQuery(id+"F6.wireOp",EDGE,"E143"),sQuery(id+"F6.wireOp",EDGE,"E144"),sQuery(id+"F6.wireOp",EDGE,"E145"),sQuery(id+"F6.wireOp",EDGE,"E146"),sQuery(id+"F6.wireOp",EDGE,"E147"),sQuery(id+"F6.wireOp",EDGE,"E148"),sQuery(id+"F6.wireOp",EDGE,"E149"),sQuery(id+"F6.wireOp",EDGE,"E150"),sQuery(id+"F6.wireOp",EDGE,"E151"),sQuery(id+"F6.wireOp",EDGE,"E152"),sQuery(id+"F6.wireOp",EDGE,"E153"),sQuery(id+"F6.wireOp",EDGE,"E154"),sQuery(id+"F6.wireOp",EDGE,"E155"),sQuery(id+"F6.wireOp",EDGE,"E156"),sQuery(id+"F6.wireOp",EDGE,"E157"),sQuery(id+"F6.wireOp",EDGE,"E158"),sQuery(id+"F6.wireOp",EDGE,"E159"),sQuery(id+"F6.wireOp",EDGE,"E160"),sQuery(id+"F6.wireOp",EDGE,"E161"),sQuery(id+"F6.wireOp",EDGE,"E162"),sQuery(id+"F6.wireOp",EDGE,"E163"),sQuery(id+"F6.wireOp",EDGE,"E164"),sQuery(id+"F6.wireOp",EDGE,"E165"),sQuery(id+"F6.wireOp",EDGE,"E166"),sQuery(id+"F6.wireOp",EDGE,"E167"),sQuery(id+"F6.wireOp",EDGE,"E168"),sQuery(id+"F6.wireOp",EDGE,"E169"),sQuery(id+"F6.wireOp",EDGE,"E170"),sQuery(id+"F6.wireOp",EDGE,"E171"),sQuery(id+"F6.wireOp",EDGE,"E172"),sQuery(id+"F6.wireOp",EDGE,"E173"),sQuery(id+"F6.wireOp",EDGE,"E174"),sQuery(id+"F6.wireOp",EDGE,"E175"),sQuery(id+"F6.wireOp",EDGE,"E176"),sQuery(id+"F6.wireOp",EDGE,"E177"),sQuery(id+"F6.wireOp",EDGE,"E178"),sQuery(id+"F6.wireOp",EDGE,"E179"),sQuery(id+"F6.wireOp",EDGE,"E180"),sQuery(id+"F6.wireOp",EDGE,"E181"),sQuery(id+"F6.wireOp",EDGE,"E182"),sQuery(id+"F6.wireOp",EDGE,"E183"),sQuery(id+"F6.wireOp",EDGE,"E184"),sQuery(id+"F6.wireOp",EDGE,"E185"),sQuery(id+"F6.wireOp",EDGE,"f9493e98-5abe-4126-86ac-bdb0b4f7d6da"),sQuery(id+"F6.wireOp",EDGE,"112f2961-29c0-47fd-bd17-f927e6cd5f86"),sQuery(id+"F6.wireOp",EDGE,"d182d45b-51f4-4f19-bbab-538119165d43"),sQuery(id+"F6.wireOp",EDGE,"f2dcc7ce-426b-4624-9908-b4b424994630")])],"isStart":false}),"instanceName":"1"});
            cPlane(context, id + "F11", {"entities" : qUnion([Q0]), "cplaneType" : CPlaneType.OFFSET, "offset" : 0 * mm, "width" : 152.4 * mm, "height" : 152.4 * mm});
        }
        {
            var Q0;
            Q0=qCreatedBy(id+"F11.planeOp",FACE);
            var sketch = newSketch(context, id + "F12", { "sketchPlane" : qUnion([Q0])});
            skLineSegment(sketch, "E192", {"start": v(122.27, 73.06) * mm, "end": v(89.92, 75.84) * mm});
            skPoint(sketch, "E192.endSnap0", {"position": v(89.92, 75.87) * mm});
            skLineSegment(sketch, "E193", {"start": v(89.92, 75.84) * mm, "end": v(99.44, 97.3) * mm});
            skLineSegment(sketch, "E194", {"start": v(99.44, 97.3) * mm, "end": v(119.46, 93.1) * mm});
            skLineSegment(sketch, "E195", {"start": v(119.46, 93.1) * mm, "end": v(122.27, 73.06) * mm});
            skSolve(sketch);
        }
        {
            var Q0;
            Q0 = qSketchRegion(id + "F12", true);
            extrude(context, id + "F13", {"entities" : qUnion([Q0]), "operationType" : NewBodyOperationType.REMOVE, "endBound" : BoundingType.THROUGH_ALL, "oppositeDirection" : true, "depth" : 70.87 * mm});
        }
        {
            var Q0;
            Q0=makeQuery(id+"F4.opExtrude","CAP_FACE",FACE,{"disambiguationData":[OSD([sQuery(id+"F3.wireOp",EDGE,"E98"),sQuery(id+"F3.wireOp",EDGE,"E99"),sQuery(id+"F3.wireOp",EDGE,"E100"),sQuery(id+"F3.wireOp",EDGE,"E101"),sQuery(id+"F3.wireOp",EDGE,"E102"),sQuery(id+"F3.wireOp",EDGE,"E103"),sQuery(id+"F3.wireOp",EDGE,"E104"),sQuery(id+"F3.wireOp",EDGE,"E105")])],"isStart":false});
            var sketch = newSketch(context, id + "F14", { "sketchPlane" : qUnion([Q0])});
            skLineSegment(sketch, "E196.bottom", {"start": v(-225.43, -101.6) * mm, "end": v(-36.83, -101.6) * mm});
            skLineSegment(sketch, "E196.top", {"start": v(-225.43, -127) * mm, "end": v(225.43, -127) * mm});
            skLineSegment(sketch, "E196.left", {"start": v(-225.43, -101.6) * mm, "end": v(-225.43, -127) * mm});
            skLineSegment(sketch, "E196.right", {"start": v(225.43, -101.6) * mm, "end": v(225.43, -127) * mm});
            skLineSegment(sketch, "E197.bottom", {"start": v(-36.83, -76.2) * mm, "end": v(39.37, -76.2) * mm});
            skLineSegment(sketch, "E197.left", {"start": v(-36.83, -76.2) * mm, "end": v(-36.83, -101.6) * mm});
            skLineSegment(sketch, "E197.right", {"start": v(39.37, -76.2) * mm, "end": v(39.37, -101.6) * mm});
            skLineSegment(sketch, "E198.trimOffspring", {"start": v(39.37, -101.6) * mm, "end": v(225.43, -101.6) * mm});
            skSolve(sketch);
        }
        {
            var Q0;
            Q0 = qSketchRegion(id + "F14", true);
            extrude(context, id + "F15", {"entities" : qUnion([Q0]), "depth" : 6.35 * mm});
        }
        {
            var Q0;
            Q0=makeQuery(id+"F15.opExtrude","CAP_FACE",FACE,{"disambiguationData":[OSD([sQuery(id+"F14.wireOp",EDGE,"E196.bottom"),sQuery(id+"F14.wireOp",EDGE,"E196.top"),sQuery(id+"F14.wireOp",EDGE,"E196.left"),sQuery(id+"F14.wireOp",EDGE,"E196.right"),sQuery(id+"F14.wireOp",EDGE,"E197.bottom"),sQuery(id+"F14.wireOp",EDGE,"E197.left"),sQuery(id+"F14.wireOp",EDGE,"E197.right"),sQuery(id+"F14.wireOp",EDGE,"E198.trimOffspring")])],"isStart":false});
            var sketch = newSketch(context, id + "F16", { "sketchPlane" : qUnion([Q0])});
            skLineSegment(sketch, "E199.bottom", {"start": v(-225.43, -101.6) * mm, "end": v(-196.22, -101.6) * mm});
            skLineSegment(sketch, "E199.top", {"start": v(-225.43, -127) * mm, "end": v(225.43, -127) * mm});
            skLineSegment(sketch, "E199.left", {"start": v(-225.43, -101.6) * mm, "end": v(-225.43, -127) * mm});
            skLineSegment(sketch, "E199.right", {"start": v(225.43, -101.6) * mm, "end": v(225.43, -127) * mm});
            skLineSegment(sketch, "E200.left", {"start": v(-196.22, -101.6) * mm, "end": v(-196.22, -91.44) * mm});
            skLineSegment(sketch, "E200.right", {"start": v(196.22, -101.6) * mm, "end": v(196.22, -91.44) * mm});
            skLineSegment(sketch, "E201.top", {"start": v(-208.92, -91.44) * mm, "end": v(-196.22, -91.44) * mm});
            skLineSegment(sketch, "E201.left", {"start": v(-208.92, -54.61) * mm, "end": v(-208.92, -91.44) * mm});
            skLineSegment(sketch, "E202.top", {"start": v(196.22, -91.44) * mm, "end": v(208.92, -91.44) * mm});
            skLineSegment(sketch, "E202.right", {"start": v(208.92, -54.61) * mm, "end": v(208.92, -91.44) * mm});
            skLineSegment(sketch, "E203.bottom", {"start": v(149.86, -11.94) * mm, "end": v(167.64, -11.94) * mm});
            skLineSegment(sketch, "E203.left", {"start": v(149.86, -11.94) * mm, "end": v(149.86, -54.6) * mm});
            skLineSegment(sketch, "E203.right", {"start": v(167.64, -11.94) * mm, "end": v(167.64, -54.61) * mm});
            skLineSegment(sketch, "E204.bottom", {"start": v(-167.9, -11.94) * mm, "end": v(-150.11, -11.94) * mm});
            skLineSegment(sketch, "E204.left", {"start": v(-167.9, -11.94) * mm, "end": v(-167.9, -54.61) * mm});
            skLineSegment(sketch, "E204.right", {"start": v(-150.11, -11.94) * mm, "end": v(-150.11, -54.61) * mm});
            skLineSegment(sketch, "E205.trimOffspring", {"start": v(-150.11, -54.61) * mm, "end": v(149.86, -54.6) * mm});
            skLineSegment(sketch, "E206.trimOffspring", {"start": v(196.22, -101.6) * mm, "end": v(225.43, -101.6) * mm});
            skLineSegment(sketch, "E207", {"start": v(-208.92, -54.61) * mm, "end": v(-167.9, -54.61) * mm});
            skLineSegment(sketch, "E208", {"start": v(208.92, -54.61) * mm, "end": v(167.64, -54.61) * mm});
            skSolve(sketch);
        }
        {
            var Q0;
            Q0 = qSketchRegion(id + "F16", true);
            extrude(context, id + "F17", {"entities" : qUnion([Q0]), "depth" : 6.35 * mm});
        }
    });
